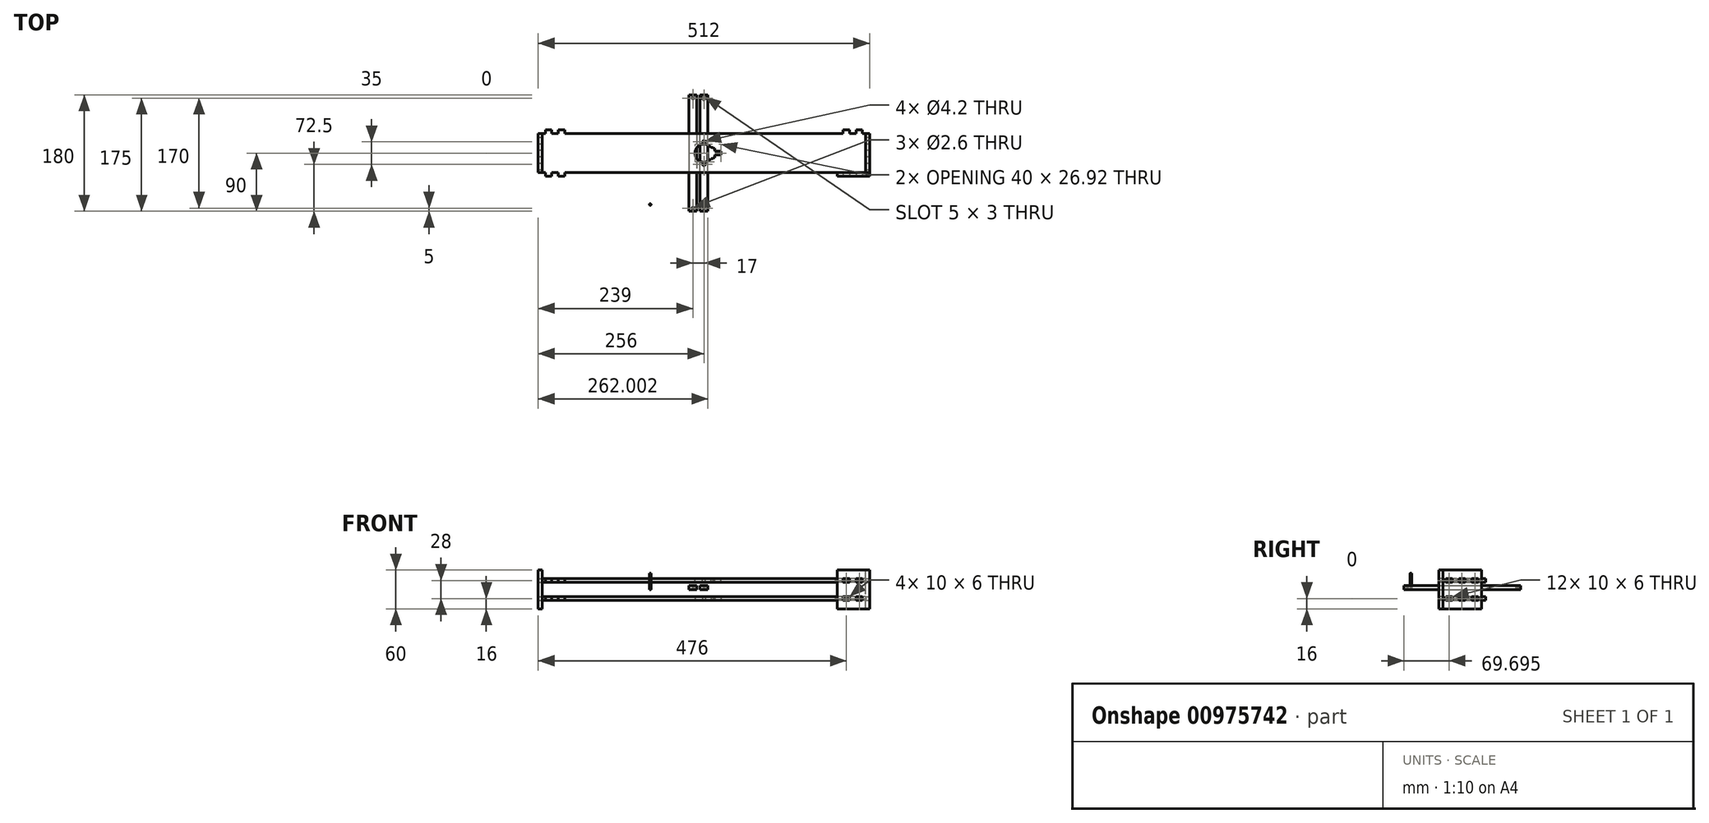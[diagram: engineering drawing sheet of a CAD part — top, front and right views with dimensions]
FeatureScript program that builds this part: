
annotation { "Feature Type Name" : "Feature", "Feature Type Description" : "" }
export const myFeature = defineFeature(function(context is Context, id is Id, definition is map)
    precondition{}
    {
        {
            var Q0;
            Q0=qCreatedBy(makeId("Top.planeOp"),FACE);
            var sketch = newSketch(context, id + "F0", { "sketchPlane" : qUnion([Q0])});
            skLineSegment(sketch, "E0.bottom", {"start": v(250, -30) * mm, "end": v(245, -30) * mm});
            skLineSegment(sketch, "E0.top", {"start": v(250, 30) * mm, "end": v(245, 30) * mm});
            skLineSegment(sketch, "E0.left", {"start": v(250, -30) * mm, "end": v(250, -25.3) * mm});
            skLineSegment(sketch, "E0.right", {"start": v(-250, -30) * mm, "end": v(-250, -25.3) * mm});
            skPoint(sketch, "E0.middle", {"position": v(0, 0) * mm});
            skCircle(sketch, "E1", {"center": v(0, 0) * mm, "radius": 14 * mm});
            skLineSegment(sketch, "E2.bottom", {"start": v(17, -7.3) * mm, "end": v(11, -7.3) * mm});
            skLineSegment(sketch, "E2.top", {"start": v(17, 7.3) * mm, "end": v(11, 7.3) * mm});
            skLineSegment(sketch, "E2.left", {"start": v(17, -7.3) * mm, "end": v(17, 7.3) * mm});
            skLineSegment(sketch, "E2.right", {"start": v(11, -7.3) * mm, "end": v(11, 7.3) * mm});
            skPoint(sketch, "E2.middle", {"position": v(14, 0) * mm});
            skLineSegment(sketch, "E3.bottom", {"start": v(14, -8.75) * mm, "end": v(8, -8.75) * mm});
            skLineSegment(sketch, "E3.top", {"start": v(14, 8.75) * mm, "end": v(8, 8.75) * mm});
            skLineSegment(sketch, "E3.left", {"start": v(14, -8.75) * mm, "end": v(14, 8.75) * mm});
            skLineSegment(sketch, "E3.right", {"start": v(8, -8.75) * mm, "end": v(8, 8.75) * mm});
            skPoint(sketch, "E3.middle", {"position": v(11, 0) * mm});
            skLineSegment(sketch, "E4.bottom", {"start": v(26, -3) * mm, "end": v(8, -3) * mm});
            skLineSegment(sketch, "E4.top", {"start": v(26, 3) * mm, "end": v(8, 3) * mm});
            skLineSegment(sketch, "E4.left", {"start": v(26, -3) * mm, "end": v(26, 3) * mm});
            skLineSegment(sketch, "E4.right", {"start": v(8, -3) * mm, "end": v(8, 3) * mm});
            skPoint(sketch, "E4.middle", {"position": v(17, 0) * mm});
            skCircle(sketch, "E5", {"center": v(0, 17.5) * mm, "radius": 2.1 * mm});
            skCircle(sketch, "E6.MirrorC", {"center": v(0, -17.5) * mm, "radius": 2.1 * mm});
            skPoint(sketch, "E7", {"position": v(250, 20) * mm});
            skLineSegment(sketch, "E8.bottom", {"start": v(256, 14.7) * mm, "end": v(250, 14.7) * mm});
            skLineSegment(sketch, "E8.top", {"start": v(256, 24.7) * mm, "end": v(250, 24.7) * mm});
            skLineSegment(sketch, "E8.left", {"start": v(256, 14.7) * mm, "end": v(256, 24.7) * mm});
            skLineSegment(sketch, "E9.trimOffspring", {"start": v(250, 24.7) * mm, "end": v(250, 30) * mm});
            skLineSegment(sketch, "E10.0.1.0", {"start": v(256, -5.3) * mm, "end": v(250, -5.3) * mm});
            skLineSegment(sketch, "E10.0.1.1", {"start": v(256, -5.3) * mm, "end": v(256, 4.7) * mm});
            skLineSegment(sketch, "E10.0.1.2", {"start": v(256, 4.7) * mm, "end": v(250, 4.7) * mm});
            skLineSegment(sketch, "E10.0.2.0", {"start": v(256, -25.3) * mm, "end": v(250, -25.3) * mm});
            skLineSegment(sketch, "E10.0.2.1", {"start": v(256, -25.3) * mm, "end": v(256, -15.3) * mm});
            skLineSegment(sketch, "E10.0.2.2", {"start": v(256, -15.3) * mm, "end": v(250, -15.3) * mm});
            skLineSegment(sketch, "E11.trimOffspring", {"start": v(250, -15.3) * mm, "end": v(250, -5.3) * mm});
            skLineSegment(sketch, "E12.trimOffspring", {"start": v(250, 4.7) * mm, "end": v(250, 14.7) * mm});
            skPoint(sketch, "E13", {"position": v(240, 30) * mm});
            skLineSegment(sketch, "E14.top", {"start": v(245, 36) * mm, "end": v(235, 36) * mm});
            skLineSegment(sketch, "E14.left", {"start": v(245, 30) * mm, "end": v(245, 36) * mm});
            skLineSegment(sketch, "E14.right", {"start": v(235, 30) * mm, "end": v(235, 36) * mm});
            skLineSegment(sketch, "E15.trimOffspring", {"start": v(235, 30) * mm, "end": v(225, 30) * mm});
            skLineSegment(sketch, "E16.1.0.0", {"start": v(225, 30) * mm, "end": v(225, 36) * mm});
            skLineSegment(sketch, "E16.1.0.1", {"start": v(225, 36) * mm, "end": v(215, 36) * mm});
            skLineSegment(sketch, "E16.1.0.2", {"start": v(215, 30) * mm, "end": v(215, 36) * mm});
            skLineSegment(sketch, "E16.direction1", {"start": v(235, 30) * mm, "end": v(225, 30) * mm, "construction": true});
            skLineSegment(sketch, "E17.trimOffspring", {"start": v(215, 30) * mm, "end": v(-215, 30) * mm});
            skLineSegment(sketch, "E18.MirrorCS", {"start": v(245, -30) * mm, "end": v(245, -36) * mm});
            skLineSegment(sketch, "E19.MirrorCS", {"start": v(235, -30) * mm, "end": v(235, -36) * mm});
            skLineSegment(sketch, "E20.MirrorCS", {"start": v(225, -30) * mm, "end": v(225, -36) * mm});
            skLineSegment(sketch, "E21.MirrorCS", {"start": v(215, -30) * mm, "end": v(215, -36) * mm});
            skLineSegment(sketch, "E22.MirrorCS", {"start": v(225, -36) * mm, "end": v(215, -36) * mm});
            skLineSegment(sketch, "E23.MirrorCS", {"start": v(245, -36) * mm, "end": v(235, -36) * mm});
            skLineSegment(sketch, "E24.MirrorCS", {"start": v(-235, 30) * mm, "end": v(-235, 36) * mm});
            skLineSegment(sketch, "E25.MirrorCS", {"start": v(-245, 36) * mm, "end": v(-235, 36) * mm});
            skLineSegment(sketch, "E26.MirrorCS", {"start": v(-235, 30) * mm, "end": v(-225, 30) * mm});
            skLineSegment(sketch, "E27.MirrorCS", {"start": v(-256, 24.7) * mm, "end": v(-250, 24.7) * mm});
            skLineSegment(sketch, "E28.MirrorCS", {"start": v(-245, 30) * mm, "end": v(-245, 36) * mm});
            skLineSegment(sketch, "E29.MirrorCS", {"start": v(-250, 30) * mm, "end": v(-245, 30) * mm});
            skLineSegment(sketch, "E30.MirrorCS", {"start": v(-250, 24.7) * mm, "end": v(-250, 30) * mm});
            skLineSegment(sketch, "E31.MirrorCS", {"start": v(-235, 30) * mm, "end": v(-225, 30) * mm, "construction": true});
            skLineSegment(sketch, "E32.MirrorCS", {"start": v(-225, 30) * mm, "end": v(-225, 36) * mm});
            skLineSegment(sketch, "E33.MirrorCS", {"start": v(-256, 14.7) * mm, "end": v(-256, 24.7) * mm});
            skLineSegment(sketch, "E34.MirrorCS", {"start": v(-250, 4.7) * mm, "end": v(-250, 14.7) * mm});
            skLineSegment(sketch, "E35.MirrorCS", {"start": v(-250, -15.3) * mm, "end": v(-250, -5.3) * mm});
            skLineSegment(sketch, "E36.MirrorCS", {"start": v(-215, 30) * mm, "end": v(-215, 36) * mm});
            skLineSegment(sketch, "E37.MirrorCS", {"start": v(-256, -15.3) * mm, "end": v(-250, -15.3) * mm});
            skLineSegment(sketch, "E38.MirrorCS", {"start": v(-245, -36) * mm, "end": v(-235, -36) * mm});
            skLineSegment(sketch, "E39.MirrorCS", {"start": v(-256, -25.3) * mm, "end": v(-256, -15.3) * mm});
            skLineSegment(sketch, "E40.MirrorCS", {"start": v(-225, -36) * mm, "end": v(-215, -36) * mm});
            skLineSegment(sketch, "E41.MirrorCS", {"start": v(-256, -25.3) * mm, "end": v(-250, -25.3) * mm});
            skLineSegment(sketch, "E42.MirrorCS", {"start": v(-225, 36) * mm, "end": v(-215, 36) * mm});
            skLineSegment(sketch, "E43.MirrorCS", {"start": v(-215, -30) * mm, "end": v(-215, -36) * mm});
            skLineSegment(sketch, "E44.MirrorCS", {"start": v(-256, 14.7) * mm, "end": v(-250, 14.7) * mm});
            skLineSegment(sketch, "E45.MirrorCS", {"start": v(-225, -30) * mm, "end": v(-225, -36) * mm});
            skLineSegment(sketch, "E46.MirrorCS", {"start": v(-256, -5.3) * mm, "end": v(-256, 4.7) * mm});
            skLineSegment(sketch, "E47.MirrorCS", {"start": v(-256, -5.3) * mm, "end": v(-250, -5.3) * mm});
            skLineSegment(sketch, "E48.MirrorCS", {"start": v(-256, 4.7) * mm, "end": v(-250, 4.7) * mm});
            skLineSegment(sketch, "E49.MirrorCS", {"start": v(-235, -30) * mm, "end": v(-235, -36) * mm});
            skLineSegment(sketch, "E50.MirrorCS", {"start": v(-245, -30) * mm, "end": v(-245, -36) * mm});
            skPoint(sketch, "E51.MirrorP", {"position": v(-240, 30) * mm});
            skPoint(sketch, "E52.MirrorP", {"position": v(-250, 20) * mm});
            skLineSegment(sketch, "E53.trimOffspring", {"start": v(215, -30) * mm, "end": v(-215, -30) * mm});
            skLineSegment(sketch, "E54.trimOffspring", {"start": v(235, -30) * mm, "end": v(225, -30) * mm});
            skLineSegment(sketch, "E55.trimOffspring", {"start": v(-245, 30) * mm, "end": v(-250, 30) * mm});
            skLineSegment(sketch, "E56.trimOffspring", {"start": v(-225, 30) * mm, "end": v(-235, 30) * mm});
            skLineSegment(sketch, "E57.trimOffspring", {"start": v(-245, -30) * mm, "end": v(-250, -30) * mm});
            skLineSegment(sketch, "E58.trimOffspring", {"start": v(-225, -30) * mm, "end": v(-235, -30) * mm});
            skSolve(sketch);
        }
        {
            var Q0;
            Q0=makeQuery(id+"F0.imprint","IMPRINT",FACE,{"disambiguationData":[TD([[makeQuery(id+"F0.imprint","IMPRINT",EDGE,{"derivedFrom":sQuery(id+"F0.wireOp",EDGE,"E0.bottom")}),-1.0]])]});
            extrude(context, id + "F1", {"entities" : qUnion([Q0]), "depth" : 6 * mm, "offsetDistance" : 25 * mm});
        }
        {
            var Q0;
            Q0=qCreatedBy(makeId("Top.planeOp"),FACE);
            cPlane(context, id + "F2", {"entities" : qUnion([Q0]), "cplaneType" : CPlaneType.OFFSET, "offset" : (11 + 6) * mm, "width" : 150 * mm, "height" : 150 * mm});
        }
        {
            var Q0;
            Q0=makeQuery(id+"F1.opExtrude","SWEPT_BODY",BODY,{"disambiguationData":[OSD([sQuery(id+"F0.wireOp",EDGE,"E0.bottom"),sQuery(id+"F0.wireOp",EDGE,"E0.top"),sQuery(id+"F0.wireOp",EDGE,"E0.left"),sQuery(id+"F0.wireOp",EDGE,"E1"),sQuery(id+"F0.wireOp",EDGE,"E2.bottom"),sQuery(id+"F0.wireOp",EDGE,"E2.top"),sQuery(id+"F0.wireOp",EDGE,"E2.left"),sQuery(id+"F0.wireOp",EDGE,"E3.bottom"),sQuery(id+"F0.wireOp",EDGE,"E3.top"),sQuery(id+"F0.wireOp",EDGE,"E3.left"),sQuery(id+"F0.wireOp",EDGE,"E4.bottom"),sQuery(id+"F0.wireOp",EDGE,"E4.top"),sQuery(id+"F0.wireOp",EDGE,"E4.left"),sQuery(id+"F0.wireOp",EDGE,"E5"),sQuery(id+"F0.wireOp",EDGE,"E6.MirrorC"),sQuery(id+"F0.wireOp",EDGE,"E8.bottom"),sQuery(id+"F0.wireOp",EDGE,"E8.top"),sQuery(id+"F0.wireOp",EDGE,"E8.left"),sQuery(id+"F0.wireOp",EDGE,"E9.trimOffspring"),sQuery(id+"F0.wireOp",EDGE,"E10.0.1.0"),sQuery(id+"F0.wireOp",EDGE,"E10.0.1.1"),sQuery(id+"F0.wireOp",EDGE,"E10.0.1.2"),sQuery(id+"F0.wireOp",EDGE,"E10.0.2.0"),sQuery(id+"F0.wireOp",EDGE,"E10.0.2.1"),sQuery(id+"F0.wireOp",EDGE,"E10.0.2.2"),sQuery(id+"F0.wireOp",EDGE,"E11.trimOffspring"),sQuery(id+"F0.wireOp",EDGE,"E12.trimOffspring"),sQuery(id+"F0.wireOp",EDGE,"E14.top"),sQuery(id+"F0.wireOp",EDGE,"E14.left"),sQuery(id+"F0.wireOp",EDGE,"E14.right"),sQuery(id+"F0.wireOp",EDGE,"E15.trimOffspring"),sQuery(id+"F0.wireOp",EDGE,"E16.1.0.0"),sQuery(id+"F0.wireOp",EDGE,"E16.1.0.1"),sQuery(id+"F0.wireOp",EDGE,"E16.1.0.2"),sQuery(id+"F0.wireOp",EDGE,"E17.trimOffspring"),sQuery(id+"F0.wireOp",EDGE,"E18.MirrorCS"),sQuery(id+"F0.wireOp",EDGE,"E19.MirrorCS"),sQuery(id+"F0.wireOp",EDGE,"E20.MirrorCS"),sQuery(id+"F0.wireOp",EDGE,"E21.MirrorCS"),sQuery(id+"F0.wireOp",EDGE,"E22.MirrorCS"),sQuery(id+"F0.wireOp",EDGE,"E23.MirrorCS"),sQuery(id+"F0.wireOp",EDGE,"E24.MirrorCS"),sQuery(id+"F0.wireOp",EDGE,"E25.MirrorCS"),sQuery(id+"F0.wireOp",EDGE,"E27.MirrorCS"),sQuery(id+"F0.wireOp",EDGE,"E28.MirrorCS"),sQuery(id+"F0.wireOp",EDGE,"E32.MirrorCS"),sQuery(id+"F0.wireOp",EDGE,"E33.MirrorCS"),sQuery(id+"F0.wireOp",EDGE,"E35.MirrorCS"),sQuery(id+"F0.wireOp",EDGE,"E36.MirrorCS"),sQuery(id+"F0.wireOp",EDGE,"E37.MirrorCS"),sQuery(id+"F0.wireOp",EDGE,"E38.MirrorCS"),sQuery(id+"F0.wireOp",EDGE,"E39.MirrorCS"),sQuery(id+"F0.wireOp",EDGE,"E0.right"),sQuery(id+"F0.wireOp",EDGE,"E40.MirrorCS"),sQuery(id+"F0.wireOp",EDGE,"E41.MirrorCS"),sQuery(id+"F0.wireOp",EDGE,"E42.MirrorCS"),sQuery(id+"F0.wireOp",EDGE,"E43.MirrorCS"),sQuery(id+"F0.wireOp",EDGE,"E44.MirrorCS"),sQuery(id+"F0.wireOp",EDGE,"E45.MirrorCS"),sQuery(id+"F0.wireOp",EDGE,"E46.MirrorCS"),sQuery(id+"F0.wireOp",EDGE,"E47.MirrorCS"),sQuery(id+"F0.wireOp",EDGE,"E48.MirrorCS"),sQuery(id+"F0.wireOp",EDGE,"E49.MirrorCS"),sQuery(id+"F0.wireOp",EDGE,"E50.MirrorCS"),sQuery(id+"F0.wireOp",EDGE,"E53.trimOffspring"),sQuery(id+"F0.wireOp",EDGE,"E54.trimOffspring"),sQuery(id+"F0.wireOp",EDGE,"E30.MirrorCS"),sQuery(id+"F0.wireOp",EDGE,"E55.trimOffspring"),sQuery(id+"F0.wireOp",EDGE,"E56.trimOffspring"),sQuery(id+"F0.wireOp",EDGE,"E34.MirrorCS"),sQuery(id+"F0.wireOp",EDGE,"E57.trimOffspring"),sQuery(id+"F0.wireOp",EDGE,"E58.trimOffspring")])]});
            var Q1;
            Q1=qCreatedBy(id+"F2.planeOp",FACE);
            mirror(context, id + "F3", {"entities" : qUnion([Q0]), "mirrorPlane" : qUnion([Q1])});
        }
        {
            var Q0;
            Q0=makeQuery(id+"F3.opPattern","COPY",FACE,{"derivedFrom":makeQuery(id+"F1.opExtrude","SWEPT_FACE",FACE,{"disambiguationData":[OSD([sQuery(id+"F0.wireOp",EDGE,"E10.0.1.1")])]}),"instanceName":"1"});
            cPlane(context, id + "F4", {"entities" : qUnion([Q0]), "cplaneType" : CPlaneType.OFFSET, "offset" : 0 * mm, "width" : 150 * mm, "height" : 150 * mm});
        }
        {
            var Q0;
            Q0=qCreatedBy(id+"F4.planeOp",FACE);
            var sketch = newSketch(context, id + "F5", { "sketchPlane" : qUnion([Q0])});
            skPoint(sketch, "E59", {"position": v(0, 17) * mm});
            skLineSegment(sketch, "E60.bottom", {"start": v(30, -13) * mm, "end": v(-30, -13) * mm});
            skLineSegment(sketch, "E60.top", {"start": v(30, 47) * mm, "end": v(-30, 47) * mm});
            skLineSegment(sketch, "E60.left", {"start": v(30, -13) * mm, "end": v(30, 47) * mm});
            skLineSegment(sketch, "E60.right", {"start": v(-30, -13) * mm, "end": v(-30, 47) * mm});
            skLineSegment(sketch, "E61.0", {"start": v(-25.3, 34) * mm, "end": v(-15.3, 34) * mm});
            skLineSegment(sketch, "E61.1", {"start": v(-25.3, 28) * mm, "end": v(-25.3, 34) * mm});
            skLineSegment(sketch, "E61.2", {"start": v(-25.3, 28) * mm, "end": v(-15.3, 28) * mm});
            skLineSegment(sketch, "E61.3", {"start": v(-15.3, 28) * mm, "end": v(-15.3, 34) * mm});
            skLineSegment(sketch, "E62.0.0", {"start": v(4.7, 34) * mm, "end": v(-5.3, 34) * mm});
            skLineSegment(sketch, "E62.0.1", {"start": v(-5.3, 34) * mm, "end": v(-5.3, 28) * mm});
            skLineSegment(sketch, "E62.0.2", {"start": v(-5.3, 28) * mm, "end": v(4.7, 28) * mm});
            skLineSegment(sketch, "E62.0.3", {"start": v(4.7, 28) * mm, "end": v(4.7, 34) * mm});
            skLineSegment(sketch, "E63.0.0", {"start": v(24.7, 34) * mm, "end": v(14.7, 34) * mm});
            skLineSegment(sketch, "E63.0.1", {"start": v(14.7, 34) * mm, "end": v(14.7, 28) * mm});
            skLineSegment(sketch, "E63.0.2", {"start": v(14.7, 28) * mm, "end": v(24.7, 28) * mm});
            skLineSegment(sketch, "E63.0.3", {"start": v(24.7, 28) * mm, "end": v(24.7, 34) * mm});
            skLineSegment(sketch, "E64.0.0", {"start": v(14.7, 0) * mm, "end": v(24.7, 0) * mm});
            skLineSegment(sketch, "E64.0.1", {"start": v(24.7, 0) * mm, "end": v(24.7, 6) * mm});
            skLineSegment(sketch, "E64.0.2", {"start": v(24.7, 6) * mm, "end": v(14.7, 6) * mm});
            skLineSegment(sketch, "E64.0.3", {"start": v(14.7, 6) * mm, "end": v(14.7, 0) * mm});
            skLineSegment(sketch, "E65.0.0", {"start": v(-5.3, 0) * mm, "end": v(4.7, 0) * mm});
            skLineSegment(sketch, "E65.0.1", {"start": v(4.7, 0) * mm, "end": v(4.7, 6) * mm});
            skLineSegment(sketch, "E65.0.2", {"start": v(4.7, 6) * mm, "end": v(-5.3, 6) * mm});
            skLineSegment(sketch, "E65.0.3", {"start": v(-5.3, 6) * mm, "end": v(-5.3, 0) * mm});
            skLineSegment(sketch, "E66.0.0", {"start": v(-25.3, 0) * mm, "end": v(-15.3, 0) * mm});
            skLineSegment(sketch, "E66.0.1", {"start": v(-15.3, 0) * mm, "end": v(-15.3, 6) * mm});
            skLineSegment(sketch, "E66.0.2", {"start": v(-15.3, 6) * mm, "end": v(-25.3, 6) * mm});
            skLineSegment(sketch, "E66.0.3", {"start": v(-25.3, 6) * mm, "end": v(-25.3, 0) * mm});
            skSolve(sketch);
        }
        {
            var Q0;
            Q0=makeQuery(id+"F5.imprint","IMPRINT",FACE,{"disambiguationData":[TD([[makeQuery(id+"F5.imprint","IMPRINT",EDGE,{"derivedFrom":sQuery(id+"F5.wireOp",EDGE,"E60.bottom")}),-1.0]])]});
            extrude(context, id + "F6", {"entities" : qUnion([Q0]), "depth" : -6 * mm, "offsetDistance" : 25 * mm});
        }
        {
            var Q0;
            Q0=makeQuery(id+"F6.opExtrude","SWEPT_BODY",BODY,{"disambiguationData":[OSD([sQuery(id+"F5.wireOp",EDGE,"E60.bottom"),sQuery(id+"F5.wireOp",EDGE,"E60.top"),sQuery(id+"F5.wireOp",EDGE,"E60.left"),sQuery(id+"F5.wireOp",EDGE,"E60.right"),sQuery(id+"F5.wireOp",EDGE,"E61.0"),sQuery(id+"F5.wireOp",EDGE,"E61.1"),sQuery(id+"F5.wireOp",EDGE,"E61.2"),sQuery(id+"F5.wireOp",EDGE,"E61.3"),sQuery(id+"F5.wireOp",EDGE,"E62.0.0"),sQuery(id+"F5.wireOp",EDGE,"E62.0.1"),sQuery(id+"F5.wireOp",EDGE,"E62.0.2"),sQuery(id+"F5.wireOp",EDGE,"E62.0.3"),sQuery(id+"F5.wireOp",EDGE,"E63.0.0"),sQuery(id+"F5.wireOp",EDGE,"E63.0.1"),sQuery(id+"F5.wireOp",EDGE,"E63.0.2"),sQuery(id+"F5.wireOp",EDGE,"E63.0.3"),sQuery(id+"F5.wireOp",EDGE,"E64.0.0"),sQuery(id+"F5.wireOp",EDGE,"E64.0.1"),sQuery(id+"F5.wireOp",EDGE,"E64.0.2"),sQuery(id+"F5.wireOp",EDGE,"E64.0.3"),sQuery(id+"F5.wireOp",EDGE,"E65.0.0"),sQuery(id+"F5.wireOp",EDGE,"E65.0.1"),sQuery(id+"F5.wireOp",EDGE,"E65.0.2"),sQuery(id+"F5.wireOp",EDGE,"E65.0.3"),sQuery(id+"F5.wireOp",EDGE,"E66.0.0"),sQuery(id+"F5.wireOp",EDGE,"E66.0.1"),sQuery(id+"F5.wireOp",EDGE,"E66.0.2"),sQuery(id+"F5.wireOp",EDGE,"E66.0.3")])]});
            var Q1;
            Q1=qCreatedBy(makeId("Right.planeOp"),FACE);
            mirror(context, id + "F7", {"entities" : qUnion([Q0]), "mirrorPlane" : qUnion([Q1])});
        }
        {
            var Q0;
            Q0=makeQuery(id+"F3.opPattern","COPY",FACE,{"derivedFrom":makeQuery(id+"F1.opExtrude","SWEPT_FACE",FACE,{"disambiguationData":[OSD([sQuery(id+"F0.wireOp",EDGE,"E23.MirrorCS")])]}),"instanceName":"1"});
            cPlane(context, id + "F8", {"entities" : qUnion([Q0]), "cplaneType" : CPlaneType.OFFSET, "offset" : 0 * mm, "width" : 150 * mm, "height" : 150 * mm});
        }
        {
            var Q0;
            Q0=qCreatedBy(id+"F8.planeOp",FACE);
            var sketch = newSketch(context, id + "F9", { "sketchPlane" : qUnion([Q0])});
            skLineSegment(sketch, "E67.0.0", {"start": v(225, 34) * mm, "end": v(215, 34) * mm});
            skLineSegment(sketch, "E67.0.1", {"start": v(215, 34) * mm, "end": v(215, 28) * mm});
            skLineSegment(sketch, "E67.0.2", {"start": v(215, 28) * mm, "end": v(225, 28) * mm});
            skLineSegment(sketch, "E67.0.3", {"start": v(225, 28) * mm, "end": v(225, 34) * mm});
            skLineSegment(sketch, "E68.0.0", {"start": v(245, 34) * mm, "end": v(235, 34) * mm});
            skLineSegment(sketch, "E68.0.1", {"start": v(235, 34) * mm, "end": v(235, 28) * mm});
            skLineSegment(sketch, "E68.0.2", {"start": v(235, 28) * mm, "end": v(245, 28) * mm});
            skLineSegment(sketch, "E68.0.3", {"start": v(245, 28) * mm, "end": v(245, 34) * mm});
            skLineSegment(sketch, "E69.0.0", {"start": v(215, 0) * mm, "end": v(225, 0) * mm});
            skLineSegment(sketch, "E69.0.1", {"start": v(225, 0) * mm, "end": v(225, 6) * mm});
            skLineSegment(sketch, "E69.0.2", {"start": v(225, 6) * mm, "end": v(215, 6) * mm});
            skLineSegment(sketch, "E69.0.3", {"start": v(215, 6) * mm, "end": v(215, 0) * mm});
            skLineSegment(sketch, "E70.0.0", {"start": v(235, 0) * mm, "end": v(245, 0) * mm});
            skLineSegment(sketch, "E70.0.1", {"start": v(245, 0) * mm, "end": v(245, 6) * mm});
            skLineSegment(sketch, "E70.0.2", {"start": v(245, 6) * mm, "end": v(235, 6) * mm});
            skLineSegment(sketch, "E70.0.3", {"start": v(235, 6) * mm, "end": v(235, 0) * mm});
            skPoint(sketch, "E71.0.2.start.orphan", {"position": v(250, 47) * mm});
            skPoint(sketch, "E71.0.3.start.orphan", {"position": v(250, -13) * mm});
            skPoint(sketch, "E71.0.0.end.orphan", {"position": v(256, 47) * mm});
            skPoint(sketch, "E71.0.0.start.orphan", {"position": v(256, -13) * mm});
            skLineSegment(sketch, "E72.bottom", {"start": v(256, 47) * mm, "end": v(206, 47) * mm});
            skLineSegment(sketch, "E72.top", {"start": v(256, -13) * mm, "end": v(206, -13) * mm});
            skLineSegment(sketch, "E72.left", {"start": v(256, 47) * mm, "end": v(256, -13) * mm});
            skLineSegment(sketch, "E72.right", {"start": v(206, 47) * mm, "end": v(206, -13) * mm});
            skSolve(sketch);
        }
        {
            var Q0;
            Q0=makeQuery(id+"F9.imprint","IMPRINT",FACE,{"disambiguationData":[TD([[makeQuery(id+"F9.imprint","IMPRINT",EDGE,{"derivedFrom":sQuery(id+"F9.wireOp",EDGE,"E67.0.0")}),-1.0]])]});
            extrude(context, id + "F10", {"entities" : qUnion([Q0]), "depth" : -6 * mm, "offsetDistance" : 25 * mm});
        }
        {
            var Q0;
            Q0=qCreatedBy(id+"F2.planeOp",FACE);
            var sketch = newSketch(context, id + "F11", { "sketchPlane" : qUnion([Q0])});
            skLineSegment(sketch, "E73.bottom", {"start": v(6, -90) * mm, "end": v(-6, -90) * mm});
            skLineSegment(sketch, "E73.top", {"start": v(6, 90) * mm, "end": v(-6, 90) * mm});
            skLineSegment(sketch, "E73.left", {"start": v(6, -90) * mm, "end": v(6, 90) * mm});
            skLineSegment(sketch, "E73.right", {"start": v(-6, -90) * mm, "end": v(-6, 90) * mm});
            skPoint(sketch, "E73.middle", {"position": v(0, 0) * mm});
            skCircle(sketch, "E74", {"center": v(0, -85) * mm, "radius": 1.3 * mm});
            skLineSegment(sketch, "E75.left", {"start": v(1.5, 83) * mm, "end": v(1.5, 87) * mm});
            skLineSegment(sketch, "E75.right", {"start": v(-1.5, 83) * mm, "end": v(-1.5, 87) * mm});
            skPoint(sketch, "E75.middle", {"position": v(0, 85) * mm});
            skArc(sketch, "E76", {"start": v(-1.5, 83) * mm, "mid": v(0, 82.5) * mm, "end": v(1.5, 83) * mm});
            skArc(sketch, "E77.trimOffspring", {"start": v(1.5, 87) * mm, "mid": v(0, 87.5) * mm, "end": v(-1.5, 87) * mm});
            skPoint(sketch, "E78.orphan", {"position": v(1.5, 87.5) * mm});
            skPoint(sketch, "E75.top.end.orphan", {"position": v(-1.5, 87.5) * mm});
            skPoint(sketch, "E79.orphan", {"position": v(-1.5, 82.5) * mm});
            skPoint(sketch, "E80.orphan", {"position": v(1.5, 82.5) * mm});
            skLineSegment(sketch, "E81.bottom", {"start": v(-11, 90) * mm, "end": v(-23, 90) * mm});
            skLineSegment(sketch, "E81.top", {"start": v(-11, -90) * mm, "end": v(-23, -90) * mm});
            skLineSegment(sketch, "E81.left", {"start": v(-11, 90) * mm, "end": v(-11, -90) * mm});
            skLineSegment(sketch, "E81.right", {"start": v(-23, 90) * mm, "end": v(-23, -90) * mm});
            skPoint(sketch, "E81.middle", {"position": v(-17, 0) * mm});
            skPoint(sketch, "E82", {"position": v(-17, -90) * mm});
            skCircle(sketch, "E83", {"center": v(-17, -85) * mm, "radius": 1.3 * mm});
            skCircle(sketch, "E84.MirrorC", {"center": v(-17, 85) * mm, "radius": 1.3 * mm});
            skSolve(sketch);
        }
        {
            var Q0;
            Q0=makeQuery(id+"F11.imprint","IMPRINT",FACE,{"disambiguationData":[TD([[makeQuery(id+"F11.imprint","IMPRINT",EDGE,{"derivedFrom":sQuery(id+"F11.wireOp",EDGE,"E81.bottom")}),1.0]])]});
            var Q1;
            Q1=makeQuery(id+"F11.imprint","IMPRINT",FACE,{"disambiguationData":[TD([[makeQuery(id+"F11.imprint","IMPRINT",EDGE,{"derivedFrom":sQuery(id+"F11.wireOp",EDGE,"E73.bottom")}),-1.0]])]});
            extrude(context, id + "F12", {"entities" : qUnion([Q0, Q1]), "depth" : 6 * mm, "offsetDistance" : 25 * mm});
        }
        {
            var Q0;
            Q0=qCreatedBy(id+"F2.planeOp",FACE);
            var sketch = newSketch(context, id + "F13", { "sketchPlane" : qUnion([Q0])});
            skCircle(sketch, "E85", {"center": v(-83.06, -79.52) * mm, "radius": 1.3 * mm});
            skSolve(sketch);
        }
        {
            var Q0;
            Q0=makeQuery(id+"F13.imprint","IMPRINT",FACE,{"disambiguationData":[TD([[makeQuery(id+"F13.imprint","IMPRINT",EDGE,{"derivedFrom":sQuery(id+"F13.wireOp",EDGE,"E85")}),1.0]])]});
            extrude(context, id + "F14", {"entities" : qUnion([Q0]), "depth" : 25 * mm, "offsetDistance" : 25 * mm});
        }
    });
